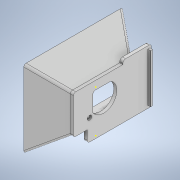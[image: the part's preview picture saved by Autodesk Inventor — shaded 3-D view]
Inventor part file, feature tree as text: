
AUTODESK INVENTOR PART (.ipt)
format: ipt  version: 2020.4 (Build 244396000, 396)  size: 914,432 bytes
history: native  units: in
note: dims shown in document units (in); Inventor stores cm internally (conversion verified against a paired STEP export)
features: sketch x34, extrude x25, projected_geometry x13, fillet x11, plane x2, loft x2, emboss x1
ambient origin geometry x8: Origin, YZ Plane, XZ Plane, XY Plane, X Axis, Y Axis, Z Axis, Center Point
bodies: Solid1 (feature_tree)
feature tree (88):
  extrude  "Extrusion1"  Depth=1.67in
  extrude  "Extrusion2"  Depth=0.8in
  sketch  "Sketch3"  dims[d4=0.4in d5=0.0in d6=1.2in]
  plane  "Work Plane1"
  sketch  "Sketch4"  dims[d7=0.5in d8=0.5in]
  sketch  "Sketch5"  dims[d9=0.28in d10=0.0in d11=1.25in d12=2.0in]
  sketch  "Sketch6"  dims[d13=2.0in d14=1.5in]
  sketch  "Sketch7"  dims[d15=1.5in d16=0.25in]
  loft  "Loft1"
  loft  "Loft2"
  extrude  "Extrusion3"  Depth=1.25in
  fillet  "Fillet1"  Radius=2.0in
  extrude  "Extrusion4"  Depth=1.5in
  sketch  "Sketch10"  dims[d24=0.0in d25=90.0deg d26=1.0in d27=0.0in]
  extrude  "Extrusion5"  Depth=0.25in
  extrude  "Extrusion6"  TaperAngle=0.0deg  [1 undecoded]
  extrude  "Extrusion7"  TaperAngle=0.0deg  [1 undecoded]
  extrude  "Extrusion8"  Depth=1.0in TaperAngle=0.0deg
  extrude  "Extrusion9"  Depth=0.125in TaperAngle=0.0deg
  fillet  "Fillet2"  [1 undecoded]
  fillet  "Fillet3"  Radius=0.25in
  sketch  "Sketch16"  dims[d50=0.15in d51=1.0in d52=0.0in d53=0.05in]
  extrude  "Extrusion10"  Depth=0.15in
  fillet  "Fillet4"  Radius=1.0in
  emboss  "Emboss1"
  extrude  "Extrusion11"  Depth=1.0in TaperAngle=0.0deg
  fillet  "Fillet5"  Radius=0.15in
  fillet  "Fillet6"  Radius=1.0in
  fillet  "Fillet7"  Radius=1.0in
  extrude  "Extrusion12"  Depth=0.05in
  extrude  "Extrusion13"  Depth=0.3in
  extrude  "Extrusion14"  Depth=0.05in TaperAngle=0.0deg
  fillet  "Fillet8"  Radius=0.05in
  extrude  "Extrusion15"  Depth=0.1in
  extrude  "Extrusion16"  Depth=0.6in
  fillet  "Fillet9"  Radius=0.1in
  fillet  "Fillet10"  Radius=0.05in
  plane  "Work Plane2"
  extrude  "Extrusion17"  Depth=0.1in
  extrude  "Extrusion18"  Depth=1.0in TaperAngle=0.0deg
  extrude  "Extrusion19"  Depth=0.125in
  extrude  "Extrusion20"  Depth=0.125in
  extrude  "Extrusion21"  Depth=0.125in TaperAngle=0.0deg
  extrude  "Extrusion22"  Depth=0.15in
  extrude  "Extrusion23"  Depth=0.125in
  fillet  "Fillet12"  Radius=0.0625in
  extrude  "Extrusion26"  Depth=0.9in TaperAngle=0.0deg
  sketch  "Sketch36"  dims[d96=0.1in]
  extrude  "Extrusion27"  Depth=0.125in
  sketch  "Sketch1"  dims[d0=2.42in d1=1.67in]
  sketch  "Sketch2"  dims[d2=0.25in d3=0.8in]
  sketch  "Sketch8"  dims[d17=0.2497in d18=0.0in d19=90.0deg]
  sketch  "Sketch9"  dims[d20=0.0in d21=90.0deg d22=0.0in d23=90.0deg]
  sketch  "Sketch11"  dims[d28=0.125in d29=1.0in d30=0.0in d31=0.0in d32=0.25in]
  sketch  "Sketch12"  dims[d33=0.15in d34=0.15in d35=1.0in d36=0.0in]
  projected_geometry  "Projected Loop1"
  projected_geometry  "Projected Loop2"
  projected_geometry  "Projected Loop3"
  sketch  "Sketch13"  dims[d37=1.0in d38=0.0in d39=1.0in d40=0.0in d41=0.15in d42=1.0in d43=0.0in d44=1.0in d45=0.0in]
  projected_geometry  "Projected Loop4"
  sketch  "Sketch14"  dims[d46=0.125in d47=0.05in]
  projected_geometry  "Projected Loop5"
  sketch  "Sketch15"  dims[d48=0.0in d49=0.3in]
  projected_geometry  "Projected Loop6"
  projected_geometry  "Projected Loop7"
  sketch  "Sketch17"  dims[d54=0.1in d55=0.0in d56=0.5in]
  sketch  "Sketch18"  dims[d57=0.5in d58=0.6in d59=0.1in d60=0.0in d61=0.05in]
  sketch  "Sketch19"  dims[d62=0.1in d63=0.1in]
  sketch  "Sketch20"  dims[d64=1.0in d65=0.0in d66=1.0in d67=0.0in]
  projected_geometry  "Projected Loop8"
  sketch  "Sketch21"  dims[d68=1.0in d69=0.0in d70=0.125in]
  sketch  "Sketch22"  dims[d71=0.25in d72=0.125in]
  sketch  "Sketch23"  dims[d73=0.25in d74=0.125in d75=0.0in]
  projected_geometry  "Projected Loop9"
  sketch  "Sketch24"  dims[d76=0.25in d77=0.15in]
  projected_geometry  "Projected Loop10"
  sketch  "Sketch26"  dims[d78=0.125in d79=0.0in d80=0.125in d81=0.0625in]
  sketch  "Sketch27"  dims[d82=-0.125in d83=0.9in d84=0.0in]
  projected_geometry  "Projected Loop12"
  sketch  "Sketch28"  dims[d85=0.125in d86=0.0in d87=0.481in]
  sketch  "Sketch29"  dims[d88=0.175in]
  sketch  "Sketch30"  dims[d89=0.37in]
  sketch  "Sketch31"  dims[d90=0.15in d91=0.0in]
  projected_geometry  "Projected Loop13"
  sketch  "Sketch32"  dims[d92=0.2in]
  projected_geometry  "Projected Loop14"
  sketch  "Sketch35"  dims[d93=1.0in d94=0.0in]
  sketch  "Sketch37"  dims[d97=0.125in d98=0.063in d99=0.125in d100=0.125in d101=0.0in d103=0.14in d104=0.0in d105=0.14in d106=0.0in d107=0.0156in d114=0.2in d115=1.0in d116=0.0in d117=0.37in d118=0.05in d119=0.0in]
note: 3 required parameter values undecoded (feature->parameter linkage not recoverable at this tier; creation-order binding heuristic only, values carry confidence <= 0.55)
